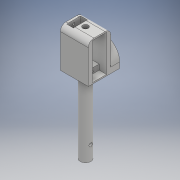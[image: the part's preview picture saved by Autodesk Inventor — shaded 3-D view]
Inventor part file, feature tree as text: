
AUTODESK INVENTOR PART (.ipt)
format: ipt  version: 2018 (Build 220112000, 112)  size: 309,760 bytes
history: native  units: mm
features: sketch x13, extrude x12, fillet x3, other x3
ambient origin geometry x8: Origin, YZ Plane, XZ Plane, XY Plane, X Axis, Y Axis, Z Axis, Center Point
bodies: Solid1 (feature_tree)
feature tree (31):
  extrude  "base"  Depth=20.0mm
  extrude  "attacher"  Depth=10.0mm
  fillet  "Fillet2"  Radius=9.5mm
  extrude  "hole_bar_rigify"  Depth=4.0mm
  extrude  "servo_place"  Depth=12.0mm TaperAngle=0.0deg
  extrude  "servo_place_2"  Depth=11.6mm
  extrude  "screw_holes"  Depth=23.2mm
  fillet  "Fillet3"  Radius=23.0mm
  extrude  "rot_axis"  Depth=4.7mm
  extrude  "cable_hole"  Depth=1.9mm
  fillet  "Fillet5"  Radius=1.9mm
  extrude  "cable_guide_1"  Depth=2.0mm
  sketch  "Sketch23"  dims[d90=6.6mm d91=0.0mm d92=20.0mm]
  sketch  "Sketch24"  dims[d93=5.0mm d94=11.0mm]
  extrude  "cable_guide_2"  Depth=20.0mm
  extrude  "cable_guide_3"  Depth=11.0mm
  other  "cable_guide_4"
  extrude  "Extrusion25"  Depth=10.0mm TaperAngle=0.0deg
  other  "Edición directa1"
  sketch  "Sketch1"  dims[d0=25.0mm d1=20.0mm]
  sketch  "Sketch4"  dims[d2=35.0mm d3=0.0mm d18=10.0mm d19=9.5mm]
  sketch  "Sketch5"  dims[d20=100.0mm d21=0.0mm d22=4.0mm]
  sketch  "Sketch15"  dims[d23=5.0mm d24=12.0mm d25=0.0mm]
  sketch  "Sketch16"  dims[d76=6.25mm d77=11.6mm]
  sketch  "Sketch17"  dims[d78=12.5mm d79=23.2mm d80=23.0mm d81=0.0mm]
  sketch  "Sketch18"  dims[d82=4.7mm d83=4.7mm]
  sketch  "Sketch21"  dims[d84=6.6mm d85=0.0mm d86=1.9mm d87=1.9mm]
  sketch  "Sketch22"  dims[d88=2.0mm d89=2.0mm]
  sketch  "Sketch25"  dims[d95=10.0mm d96=8.0mm d97=0.0mm]
  sketch  "Sketch26"  dims[d105=6.0mm d106=10.0mm d107=0.0mm d108=6.0mm d109=10.0mm d110=5.0mm d111=5.0mm d112=5.0mm d113=5.0mm d114=15.0mm d115=15.0mm d116=5.0mm d117=15.0mm d118=8.0mm d119=0.0mm d120=2.0mm d121=11.0mm d122=7.0mm d123=2.0mm d124=11.0mm d125=7.0mm d126=8.0mm d127=0.0mm d128=8.0mm d129=0.0mm d130=90.0deg d131=13.0mm d132=3.0mm d133=10.0mm d134=0.0mm d135=0.0mm d136=0.0mm d137=-33.0mm]
  other  "Desplazar1"
